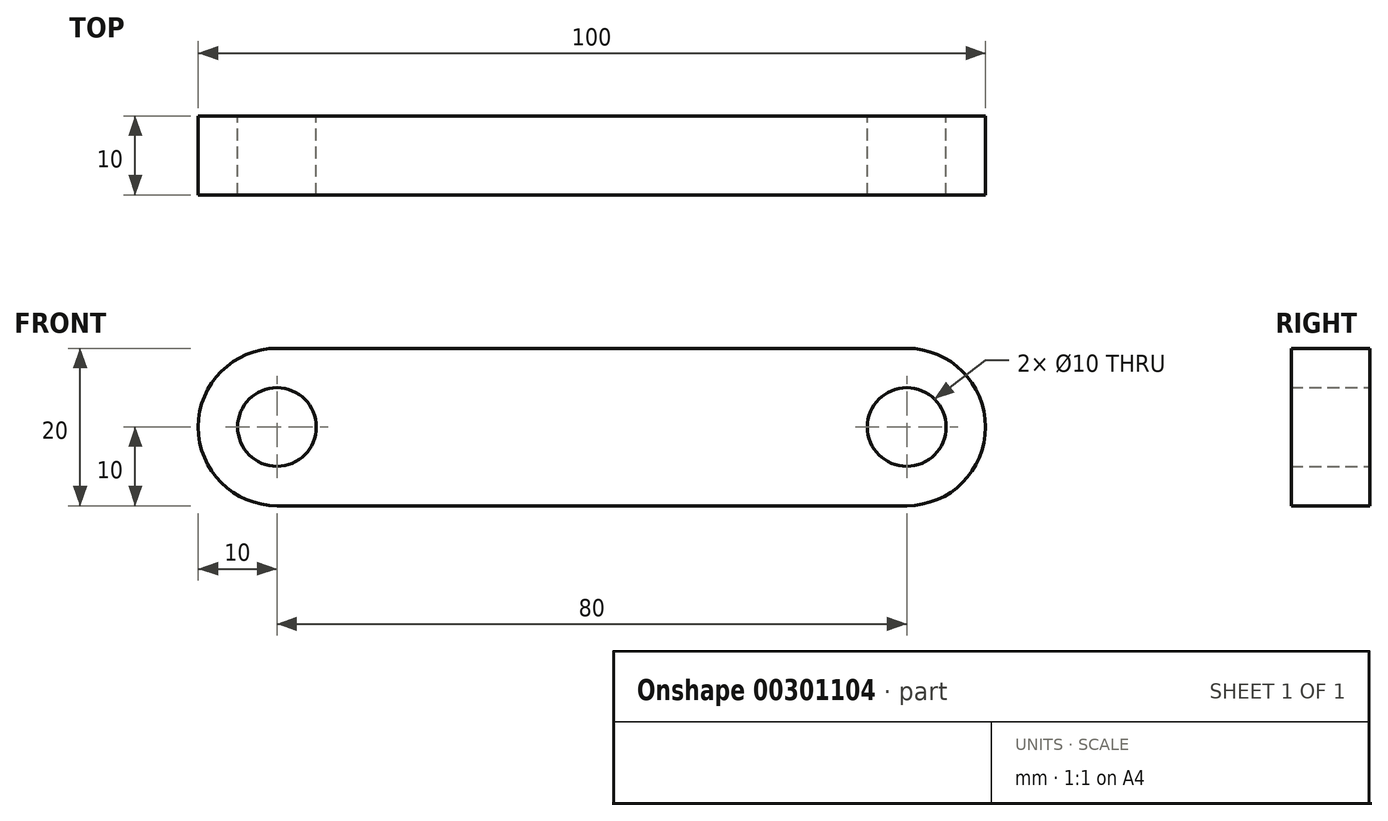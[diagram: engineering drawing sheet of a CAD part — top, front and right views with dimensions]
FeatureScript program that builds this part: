
annotation { "Feature Type Name" : "Feature", "Feature Type Description" : "" }
export const myFeature = defineFeature(function(context is Context, id is Id, definition is map)
    precondition{}
    {
        {
            var Q0;
            Q0=qCreatedBy(makeId("Front.planeOp"),FACE);
            var sketch = newSketch(context, id + "F0", { "sketchPlane" : qUnion([Q0])});
            skLineSegment(sketch, "E0.bottom", {"start": v(10, 0) * mm, "end": v(90, 0) * mm});
            skLineSegment(sketch, "E0.top", {"start": v(10, 20) * mm, "end": v(90, 20) * mm});
            skLineSegment(sketch, "E0.left", {"start": v(0, 10) * mm, "end": v(0, 10) * mm});
            skLineSegment(sketch, "E0.right", {"start": v(100, 10) * mm, "end": v(100, 10) * mm});
            skPoint(sketch, "E1.visualSharp", {"position": v(0, 20) * mm});
            skArc(sketch, "E1.filletArc", {"start": v(10, 20) * mm, "mid": v(2.93, 17.07) * mm, "end": v(0, 10) * mm});
            skPoint(sketch, "E2.visualSharp", {"position": v(0, 0) * mm});
            skArc(sketch, "E2.filletArc", {"start": v(0, 10) * mm, "mid": v(2.93, 2.93) * mm, "end": v(10, 0) * mm});
            skPoint(sketch, "E3.visualSharp", {"position": v(100, 0) * mm});
            skArc(sketch, "E3.filletArc", {"start": v(90, 0) * mm, "mid": v(97.07, 2.93) * mm, "end": v(100, 10) * mm});
            skPoint(sketch, "E4.visualSharp", {"position": v(100, 20) * mm});
            skArc(sketch, "E4.filletArc", {"start": v(100, 10) * mm, "mid": v(97.07, 17.07) * mm, "end": v(90, 20) * mm});
            skCircle(sketch, "E5", {"center": v(10, 10) * mm, "radius": 5 * mm});
            skCircle(sketch, "E6", {"center": v(90, 10) * mm, "radius": 5 * mm});
            skSolve(sketch);
        }
        {
            var Q0;
            Q0 = qSketchRegion(id + "F0", true);
            extrude(context, id + "F1", {"entities" : qUnion([Q0]), "depth" : 10 * mm});
        }
    });
